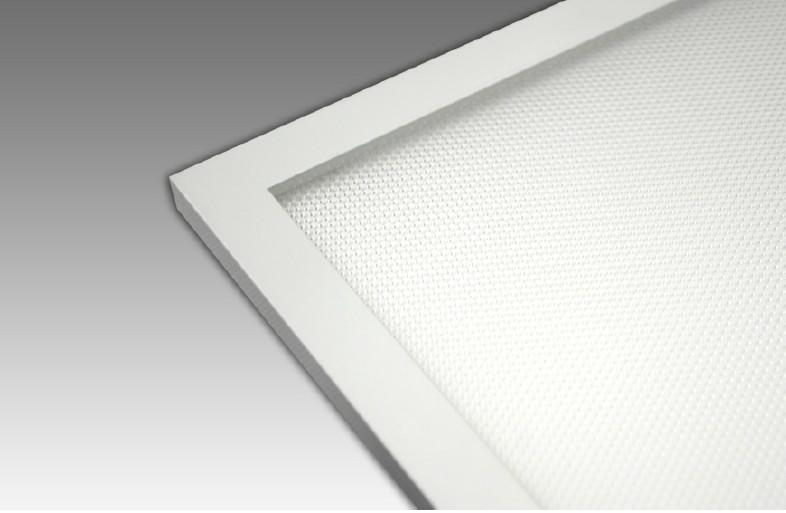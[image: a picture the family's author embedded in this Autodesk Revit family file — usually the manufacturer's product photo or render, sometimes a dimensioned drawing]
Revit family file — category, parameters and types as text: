
# Revit family: DG1012MGW
name_source: partatom
category: Lighting Fixtures
revit_build: Autodesk Revit 2017 (Build: 20160225_1515(x64)
units: mm (PartAtom-declared; Revit-internal decimal feet)

## family parameters
Cut with Voids When Loaded = No
Host = Face
Light Source = Yes
Part Type = Normal
Room Calculation Point = No
Round Connector Dimension = Use Diameter
Shared = No

## types (2) — shared parameters
Color Filter = 16777215
Default Elevation = 1219 mm
Dimming Lamp Color Temperature Shift = <None>
Emit Shape Visible in Rendering = Yes
Emit from Circle Diameter = 79 mm
Lamp = LED
Manufacturer = ARLIGHT
Model = DG1012MGW
Tilt Angle = 90.00°
Type Comments = DOWNLIGHT
Type Image = <None>

## per-type parameters (varying)
| type | Apparent Load | Photometric Web File | Wattage Comments |
| DGMGW.120.7.40 | 7 VA | dg-1012-mgw-7w-4k-sg.ies | 7 |
| DGMGW.120.10.40 | 10 VA | dg-1012-mow-10w-4k-sg.ies | 10 |

## geometry (parser evidence)
native form markers: Sweep x3
no freeform markers — native parametric forms only
